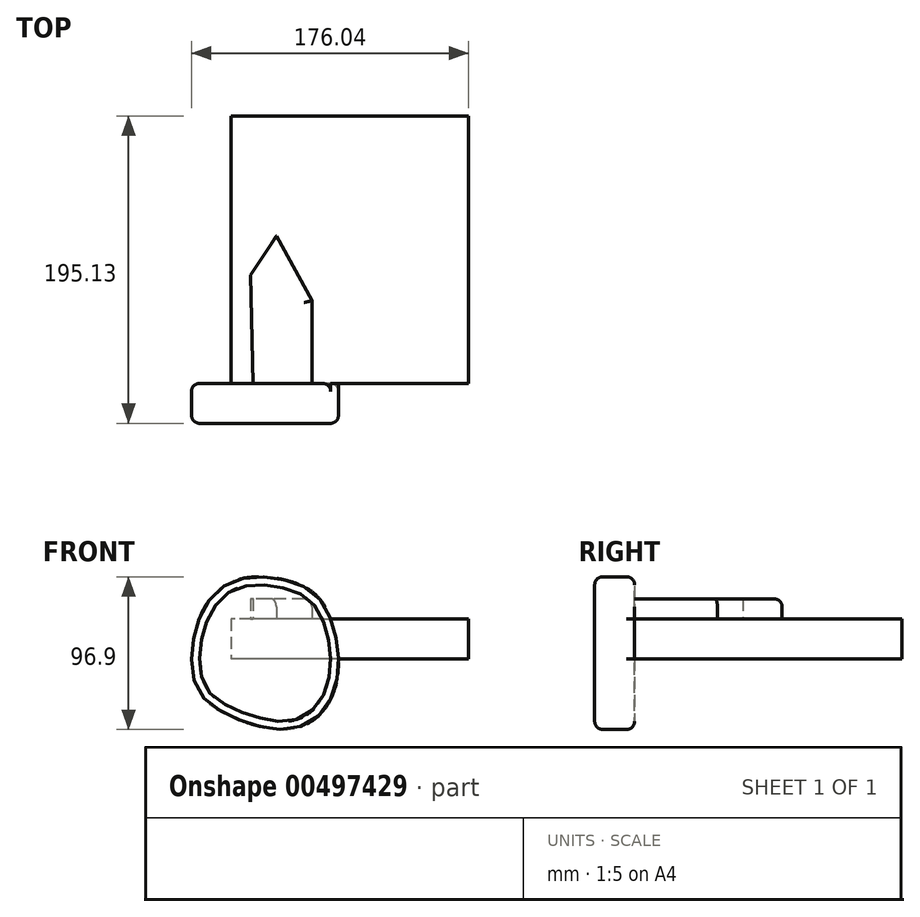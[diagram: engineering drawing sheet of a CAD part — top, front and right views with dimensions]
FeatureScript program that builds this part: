
annotation { "Feature Type Name" : "Feature", "Feature Type Description" : "" }
export const myFeature = defineFeature(function(context is Context, id is Id, definition is map)
    precondition{}
    {
        {
            var Q0;
            Q0=qCreatedBy(makeId("Front.planeOp"),FACE);
            var sketch = newSketch(context, id + "F0", { "sketchPlane" : qUnion([Q0])});
            skFitSpline(sketch, "E0", {"points": [v(-41.84, 25.5) * mm, v(-18.15, 50.1) * mm, v(22.05, 47.1) * mm, v(40.34, 28.8) * mm, v(44.84, -16.95) * mm, v(19.8, -43.8) * mm, v(-25.05, -34.65) * mm, v(-44.54, -15.3) * mm, v(-41.84, 25.5) * mm]});
            skSolve(sketch);
        }
        {
            var Q0;
            Q0=makeQuery(id+"F0.imprint","IMPRINT",FACE,{"disambiguationData":[TD([[makeQuery(id+"F0.imprint","IMPRINT",EDGE,{"derivedFrom":sQuery(id+"F0.wireOp",EDGE,"E0")}),-1.0]])]});
            extrude(context, id + "F1", {"entities" : qUnion([Q0]), "depth" : 25.4 * mm});
        }
        {
            var Q0;
            Q0=qCreatedBy(makeId("Top.planeOp"),FACE);
            var sketch = newSketch(context, id + "F2", { "sketchPlane" : qUnion([Q0])});
            skLineSegment(sketch, "E1.bottom", {"start": v(129.36, 0) * mm, "end": v(-21.52, 0) * mm});
            skLineSegment(sketch, "E1.top", {"start": v(129.36, 169.73) * mm, "end": v(-21.52, 169.73) * mm});
            skLineSegment(sketch, "E1.left", {"start": v(129.36, 0) * mm, "end": v(129.36, 169.73) * mm});
            skLineSegment(sketch, "E1.right", {"start": v(-21.52, 0) * mm, "end": v(-21.52, 169.73) * mm});
            skSolve(sketch);
        }
        {
            var Q0;
            Q0=makeQuery(id+"F2.imprint","IMPRINT",FACE,{"disambiguationData":[TD([[makeQuery(id+"F2.imprint","IMPRINT",EDGE,{"derivedFrom":sQuery(id+"F2.wireOp",EDGE,"E1.bottom")}),-1.0]])]});
            extrude(context, id + "F3", {"entities" : qUnion([Q0]), "operationType" : NewBodyOperationType.ADD, "depth" : 25.4 * mm});
        }
        {
            var Q0;
            Q0=makeQuery(id+"F3.opExtrude","CAP_FACE",FACE,{"disambiguationData":[OSD([sQuery(id+"F2.wireOp",EDGE,"E1.bottom"),sQuery(id+"F2.wireOp",EDGE,"E1.top"),sQuery(id+"F2.wireOp",EDGE,"E1.left"),sQuery(id+"F2.wireOp",EDGE,"E1.right")])],"isStart":false});
            var sketch = newSketch(context, id + "F4", { "sketchPlane" : qUnion([Q0])});
            skLineSegment(sketch, "E2", {"start": v(-7.54, 0) * mm, "end": v(29.76, 0) * mm});
            skLineSegment(sketch, "E3", {"start": v(29.76, 0) * mm, "end": v(29.76, 52.53) * mm});
            skLineSegment(sketch, "E4", {"start": v(29.76, 52.53) * mm, "end": v(7.2, 93.7) * mm});
            skLineSegment(sketch, "E5", {"start": v(7.2, 93.7) * mm, "end": v(-9.14, 68.85) * mm});
            skLineSegment(sketch, "E6", {"start": v(-9.14, 68.85) * mm, "end": v(-7.54, 0) * mm});
            skSolve(sketch);
        }
        {
            var Q0;
            Q0=makeQuery(id+"F4.imprint","IMPRINT",FACE,{"disambiguationData":[TD([[makeQuery(id+"F4.imprint","IMPRINT",EDGE,{"derivedFrom":sQuery(id+"F4.wireOp",EDGE,"E2")}),-1.0]])]});
            extrude(context, id + "F5", {"entities" : qUnion([Q0]), "operationType" : NewBodyOperationType.ADD, "depth" : 12.7 * mm});
        }
        {
            var Q0;
            Q0=makeQuery(id+"F5.opExtrude","CAP_EDGE",EDGE,{"disambiguationData":[OSD([sQuery(id+"F4.wireOp",EDGE,"E3")])],"isStart":false});
            var Q1;
            Q1=makeQuery(id+"F5.opExtrude","CAP_EDGE",EDGE,{"disambiguationData":[OSD([sQuery(id+"F4.wireOp",EDGE,"E3")])],"isStart":true});
            var Q2;
            Q2=makeQuery(id+"F5.opExtrude","CAP_EDGE",EDGE,{"disambiguationData":[OSD([sQuery(id+"F4.wireOp",EDGE,"E4")])],"isStart":true});
            var Q3;
            Q3=makeQuery(id+"F5.opExtrude","CAP_EDGE",EDGE,{"disambiguationData":[OSD([sQuery(id+"F4.wireOp",EDGE,"E4")])],"isStart":false});
            fillet(context, id + "F6", {"entities" : qUnion([Q0, Q1, Q2, Q3]), "radius" : 5.08 * mm, "tangentPropagation" : true, "allowEdgeOverflow" : false});
        }
        {
            var Q0;
            {var subQ0=sQuery(id+"F0.wireOp",EDGE,"E0");Q0=makeQuery(id+"F3.boolean.opBoolean","SPLIT",EDGE,{"disambiguationData":[topologyDisambiguationEdgeConnected([makeQuery(id+"F1.opExtrude","CAP_FACE",FACE,{"disambiguationData":[OSD([subQ0])],"isStart":true})])],"derivedFrom":makeQuery(id+"F1.opExtrude","CAP_EDGE",EDGE,{"disambiguationData":[OSD([subQ0])],"isStart":true})});}
            fillet(context, id + "F7", {"entities" : qUnion([Q0]), "radius" : 5.08 * mm, "tangentPropagation" : true, "allowEdgeOverflow" : false});
        }
        {
            var Q0;
            Q0=makeQuery(id+"F1.opExtrude","CAP_FACE",FACE,{"disambiguationData":[OSD([sQuery(id+"F0.wireOp",EDGE,"E0")])],"isStart":false});
            fillet(context, id + "F8", {"entities" : qUnion([Q0]), "radius" : 5.08 * mm, "tangentPropagation" : true, "allowEdgeOverflow" : false});
        }
    });
